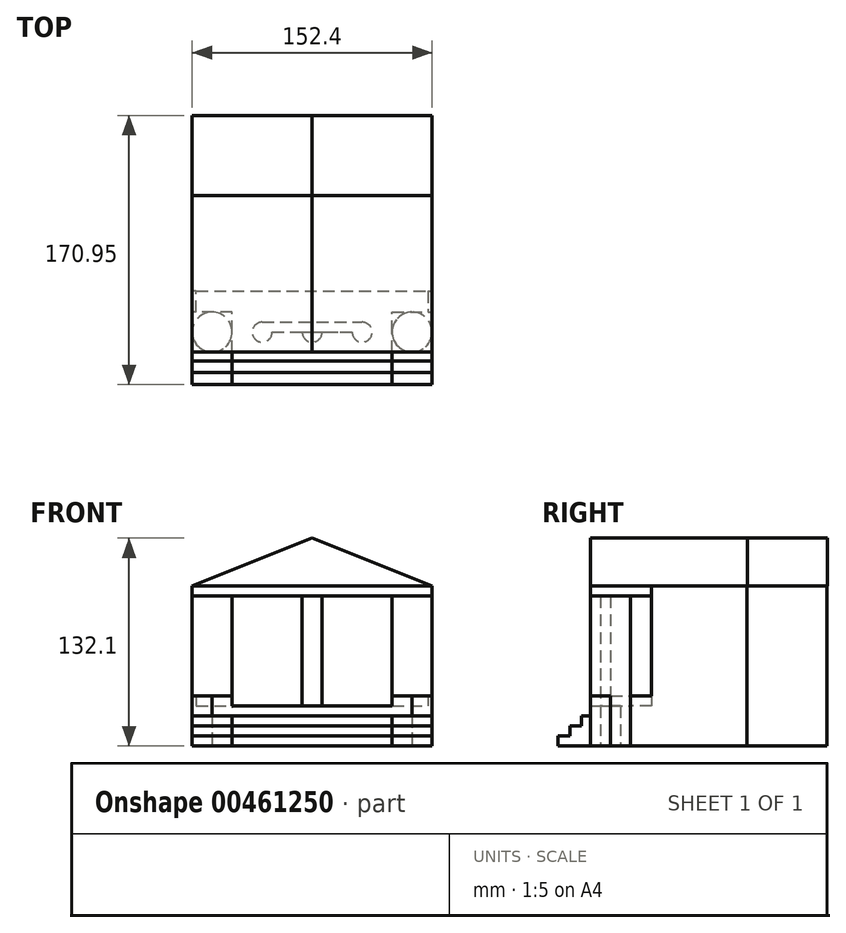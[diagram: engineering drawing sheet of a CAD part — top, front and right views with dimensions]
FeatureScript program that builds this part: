
annotation { "Feature Type Name" : "Feature", "Feature Type Description" : "" }
export const myFeature = defineFeature(function(context is Context, id is Id, definition is map)
    precondition{}
    {
        {
            var Q0;
            Q0=qCreatedBy(makeId("Top.planeOp"),FACE);
            var sketch = newSketch(context, id + "F0", { "sketchPlane" : qUnion([Q0])});
            skLineSegment(sketch, "E0.bottom", {"start": v(76.2, 49.62) * mm, "end": v(-76.2, 49.62) * mm});
            skLineSegment(sketch, "E0.top", {"start": v(76.2, -49.62) * mm, "end": v(-76.2, -49.62) * mm});
            skLineSegment(sketch, "E0.left", {"start": v(76.2, 49.62) * mm, "end": v(76.2, -49.62) * mm});
            skLineSegment(sketch, "E0.right", {"start": v(-76.2, 49.62) * mm, "end": v(-76.2, -49.62) * mm});
            skPoint(sketch, "E0.middle", {"position": v(0, 0) * mm});
            skLineSegment(sketch, "E1", {"start": v(0, -49.62) * mm, "end": v(0, 49.62) * mm});
            skLineSegment(sketch, "E2", {"start": v(-76.2, -49.62) * mm, "end": v(-50.8, -49.62) * mm});
            skLineSegment(sketch, "E3", {"start": v(76.2, -49.62) * mm, "end": v(50.8, -49.62) * mm});
            skLineSegment(sketch, "E4", {"start": v(-50.8, -49.62) * mm, "end": v(-50.8, -70.26) * mm});
            skLineSegment(sketch, "E5", {"start": v(-50.8, -70.26) * mm, "end": v(50.8, -70.26) * mm});
            skLineSegment(sketch, "E6", {"start": v(50.8, -49.62) * mm, "end": v(50.8, -70.26) * mm});
            skLineSegment(sketch, "E7", {"start": v(-50.8, -62.64) * mm, "end": v(50.8, -62.64) * mm});
            skLineSegment(sketch, "E8", {"start": v(50.8, -62.64) * mm, "end": v(50.8, -55.32) * mm});
            skLineSegment(sketch, "E9", {"start": v(50.8, -55.32) * mm, "end": v(-50.8, -55.32) * mm});
            skLineSegment(sketch, "E10", {"start": v(-50.8, -49.62) * mm, "end": v(-50.8, -24.22) * mm});
            skLineSegment(sketch, "E11", {"start": v(-50.8, -24.22) * mm, "end": v(-76.2, -24.22) * mm});
            skLineSegment(sketch, "E12", {"start": v(-76.2, -24.22) * mm, "end": v(-76.2, -49.62) * mm});
            skLineSegment(sketch, "E13", {"start": v(50.8, -49.62) * mm, "end": v(50.8, -24.22) * mm});
            skLineSegment(sketch, "E14", {"start": v(50.8, -24.22) * mm, "end": v(76.2, -24.22) * mm});
            skLineSegment(sketch, "E15", {"start": v(76.2, -24.22) * mm, "end": v(76.2, -49.62) * mm});
            skCircle(sketch, "E16", {"center": v(-63.5, -36.92) * mm, "radius": 12.7 * mm});
            skCircle(sketch, "E17", {"center": v(63.5, -36.92) * mm, "radius": 12.7 * mm});
            skLineSegment(sketch, "E18", {"start": v(-63.5, -36.92) * mm, "end": v(63.5, -36.92) * mm});
            skLineSegment(sketch, "E19", {"start": v(0, -36.92) * mm, "end": v(-63.5, -36.92) * mm});
            skLineSegment(sketch, "E20", {"start": v(-31.75, -36.92) * mm, "end": v(-31.75, -24.23) * mm});
            skLineSegment(sketch, "E21", {"start": v(0, -36.92) * mm, "end": v(63.5, -36.92) * mm});
            skLineSegment(sketch, "E22", {"start": v(31.75, -36.92) * mm, "end": v(31.75, -24.23) * mm});
            skLineSegment(sketch, "E23", {"start": v(-31.75, -30.58) * mm, "end": v(31.75, -30.58) * mm});
            skCircle(sketch, "E24", {"center": v(-31.75, -36.92) * mm, "radius": 6.35 * mm});
            skCircle(sketch, "E25", {"center": v(31.75, -36.92) * mm, "radius": 6.35 * mm});
            skCircle(sketch, "E26", {"center": v(0, -36.92) * mm, "radius": 6.35 * mm});
            skLineSegment(sketch, "E27", {"start": v(-73.66, -24.22) * mm, "end": v(-73.66, -10.82) * mm});
            skLineSegment(sketch, "E28", {"start": v(-73.66, -10.82) * mm, "end": v(73.66, -10.82) * mm});
            skLineSegment(sketch, "E29", {"start": v(73.66, -10.82) * mm, "end": v(73.66, -24.22) * mm});
            skLineSegment(sketch, "E30", {"start": v(-73.66, -24.22) * mm, "end": v(-76.2, -24.22) * mm});
            skLineSegment(sketch, "E31", {"start": v(73.66, -24.22) * mm, "end": v(76.2, -24.22) * mm});
            skLineSegment(sketch, "E32", {"start": v(73.66, -10.82) * mm, "end": v(76.2, -10.82) * mm});
            skLineSegment(sketch, "E33", {"start": v(-73.66, -10.82) * mm, "end": v(-76.2, -10.82) * mm});
            skSolve(sketch);
        }
        {
            var Q0;
            {var subQ7=sQuery(id+"F0.wireOp",EDGE,"E33");Q0=makeQuery(id+"F0.imprint","IMPRINT",FACE,{"disambiguationData":[TD([[makeQuery(id+"F0.imprint","IMPRINT",EDGE,{"derivedFrom":subQ7}),-1.0]])]});}
            var Q1;
            {var subQ0=sQuery(id+"F0.wireOp",EDGE,"E32");Q1=makeQuery(id+"F0.imprint","IMPRINT",FACE,{"disambiguationData":[TD([[makeQuery(id+"F0.imprint","IMPRINT",EDGE,{"derivedFrom":subQ0}),1.0]])]});}
            extrude(context, id + "F1", {"entities" : qUnion([Q0, Q1]), "depth" : 101.6 * mm});
        }
        {
            var Q0;
            {var subQ0=sQuery(id+"F0.wireOp",EDGE,"E27");Q0=makeQuery(id+"F0.imprint","IMPRINT",FACE,{"disambiguationData":[TD([[makeQuery(id+"F0.imprint","IMPRINT",EDGE,{"derivedFrom":subQ0}),-1.0]])]});}
            var Q1;
            {var subQ0=sQuery(id+"F0.wireOp",EDGE,"E26");var subQ1=sQuery(id+"F0.wireOp",EDGE,"E19");var subQ2=makeQuery(id+"F0.imprint","INTERSECT",VERTEX,{"derivedFrom":[subQ1,subQ0]});Q1=makeQuery(id+"F0.imprint","IMPRINT",FACE,{"disambiguationData":[TD([[makeQuery(id+"F0.imprint","IMPRINT",EDGE,{"disambiguationData":[TD([[subQ2,-1.0]])],"derivedFrom":subQ1}),-1.0]])]});}
            var Q2;
            {var subQ6=sQuery(id+"F0.wireOp",EDGE,"E0.top");var subQ8=sQuery(id+"F0.wireOp",EDGE,"E1");var subQ9=makeQuery(id+"F0.imprint","INTERSECT",VERTEX,{"derivedFrom":[subQ6,subQ8]});Q2=makeQuery(id+"F0.imprint","IMPRINT",FACE,{"disambiguationData":[TD([[makeQuery(id+"F0.imprint","IMPRINT",EDGE,{"disambiguationData":[TD([[subQ9,-1.0]])],"derivedFrom":subQ8}),1.0]])]});}
            var Q3;
            {var subQ5=sQuery(id+"F0.wireOp",EDGE,"E1");var subQ6=sQuery(id+"F0.wireOp",EDGE,"E0.top");var subQ7=makeQuery(id+"F0.imprint","INTERSECT",VERTEX,{"derivedFrom":[subQ6,subQ5]});Q3=makeQuery(id+"F0.imprint","IMPRINT",FACE,{"disambiguationData":[TD([[makeQuery(id+"F0.imprint","IMPRINT",EDGE,{"disambiguationData":[TD([[subQ7,-1.0]])],"derivedFrom":subQ5}),-1.0]])]});}
            var Q4;
            {var subQ0=sQuery(id+"F0.wireOp",EDGE,"E26");var subQ1=sQuery(id+"F0.wireOp",EDGE,"E21");var subQ2=makeQuery(id+"F0.imprint","INTERSECT",VERTEX,{"derivedFrom":[subQ1,subQ0]});Q4=makeQuery(id+"F0.imprint","IMPRINT",FACE,{"disambiguationData":[TD([[makeQuery(id+"F0.imprint","IMPRINT",EDGE,{"disambiguationData":[TD([[subQ2,-1.0]])],"derivedFrom":subQ1}),1.0]])]});}
            var Q5;
            {var subQ0=sQuery(id+"F0.wireOp",EDGE,"E29");Q5=makeQuery(id+"F0.imprint","IMPRINT",FACE,{"disambiguationData":[TD([[makeQuery(id+"F0.imprint","IMPRINT",EDGE,{"derivedFrom":subQ0}),-1.0]])]});}
            extrude(context, id + "F2", {"entities" : qUnion([Q0, Q1, Q2, Q3, Q4, Q5]), "operationType" : NewBodyOperationType.ADD, "depth" : 25.4 * mm});
        }
        {
            var Q0;
            Q0=makeQuery(id+"F0.imprint","IMPRINT",FACE,{"disambiguationData":[TD([[makeQuery(id+"F0.imprint","IMPRINT",EDGE,{"derivedFrom":sQuery(id+"F0.wireOp",EDGE,"E27")}),1.0]])]});
            var Q1;
            Q1=makeQuery(id+"F0.imprint","IMPRINT",FACE,{"disambiguationData":[TD([[makeQuery(id+"F0.imprint","IMPRINT",EDGE,{"derivedFrom":sQuery(id+"F0.wireOp",EDGE,"E29")}),1.0]])]});
            extrude(context, id + "F3", {"entities" : qUnion([Q0, Q1]), "operationType" : NewBodyOperationType.ADD, "depth" : 31.75 * mm});
        }
        {
            var Q0;
            {var subQ0=sQuery(id+"F0.wireOp",EDGE,"E19");var subQ1=makeQuery(id+"F0.imprint","INTERSECT",VERTEX,{"derivedFrom":[subQ0,sQuery(id+"F0.wireOp",EDGE,"E20")]});Q0=makeQuery(id+"F0.imprint","IMPRINT",FACE,{"disambiguationData":[TD([[makeQuery(id+"F0.imprint","IMPRINT",EDGE,{"disambiguationData":[TD([[subQ1,1.0]])],"derivedFrom":subQ0}),1.0]])]});}
            var Q1;
            {var subQ0=sQuery(id+"F0.wireOp",EDGE,"E20");var subQ1=sQuery(id+"F0.wireOp",EDGE,"E19");var subQ2=makeQuery(id+"F0.imprint","INTERSECT",VERTEX,{"derivedFrom":[subQ1,subQ0]});Q1=makeQuery(id+"F0.imprint","IMPRINT",FACE,{"disambiguationData":[TD([[makeQuery(id+"F0.imprint","IMPRINT",EDGE,{"disambiguationData":[TD([[subQ2,-1.0]])],"derivedFrom":subQ1}),-1.0]])]});}
            var Q2;
            {var subQ0=sQuery(id+"F0.wireOp",EDGE,"E20");var subQ1=sQuery(id+"F0.wireOp",EDGE,"E19");var subQ2=makeQuery(id+"F0.imprint","INTERSECT",VERTEX,{"derivedFrom":[subQ1,subQ0]});Q2=makeQuery(id+"F0.imprint","IMPRINT",FACE,{"disambiguationData":[TD([[makeQuery(id+"F0.imprint","IMPRINT",EDGE,{"disambiguationData":[TD([[subQ2,1.0]])],"derivedFrom":subQ1}),-1.0]])]});}
            var Q3;
            {var subQ0=sQuery(id+"F0.wireOp",EDGE,"E19");var subQ3=sQuery(id+"F0.wireOp",EDGE,"E26");var subQ5=makeQuery(id+"F0.imprint","INTERSECT",VERTEX,{"derivedFrom":[subQ0,subQ3]});Q3=makeQuery(id+"F0.imprint","IMPRINT",FACE,{"disambiguationData":[TD([[makeQuery(id+"F0.imprint","IMPRINT",EDGE,{"disambiguationData":[TD([[subQ5,1.0]])],"derivedFrom":subQ0}),-1.0]])]});}
            var Q4;
            {var subQ0=sQuery(id+"F0.wireOp",EDGE,"E21");var subQ3=sQuery(id+"F0.wireOp",EDGE,"E26");var subQ5=makeQuery(id+"F0.imprint","INTERSECT",VERTEX,{"derivedFrom":[subQ0,subQ3]});Q4=makeQuery(id+"F0.imprint","IMPRINT",FACE,{"disambiguationData":[TD([[makeQuery(id+"F0.imprint","IMPRINT",EDGE,{"disambiguationData":[TD([[subQ5,1.0]])],"derivedFrom":subQ0}),1.0]])]});}
            var Q5;
            {var subQ1=sQuery(id+"F0.wireOp",EDGE,"E1");var subQ3=sQuery(id+"F0.wireOp",EDGE,"E26");var subQ4=makeQuery(id+"F0.imprint","INTERSECT",VERTEX,{"derivedFrom":[subQ1,subQ3]});Q5=makeQuery(id+"F0.imprint","IMPRINT",FACE,{"disambiguationData":[TD([[makeQuery(id+"F0.imprint","IMPRINT",EDGE,{"disambiguationData":[TD([[subQ4,1.0]])],"derivedFrom":subQ3}),1.0]])]});}
            var Q6;
            {var subQ1=sQuery(id+"F0.wireOp",EDGE,"E1");var subQ3=sQuery(id+"F0.wireOp",EDGE,"E26");var subQ4=makeQuery(id+"F0.imprint","INTERSECT",VERTEX,{"derivedFrom":[subQ1,subQ3]});Q6=makeQuery(id+"F0.imprint","IMPRINT",FACE,{"disambiguationData":[TD([[makeQuery(id+"F0.imprint","IMPRINT",EDGE,{"disambiguationData":[TD([[subQ4,-1.0]])],"derivedFrom":subQ3}),1.0]])]});}
            var Q7;
            {var subQ0=sQuery(id+"F0.wireOp",EDGE,"E22");var subQ1=sQuery(id+"F0.wireOp",EDGE,"E21");var subQ2=makeQuery(id+"F0.imprint","INTERSECT",VERTEX,{"derivedFrom":[subQ1,subQ0]});Q7=makeQuery(id+"F0.imprint","IMPRINT",FACE,{"disambiguationData":[TD([[makeQuery(id+"F0.imprint","IMPRINT",EDGE,{"disambiguationData":[TD([[subQ2,1.0]])],"derivedFrom":subQ1}),1.0]])]});}
            var Q8;
            {var subQ0=sQuery(id+"F0.wireOp",EDGE,"E22");var subQ1=sQuery(id+"F0.wireOp",EDGE,"E21");var subQ2=makeQuery(id+"F0.imprint","INTERSECT",VERTEX,{"derivedFrom":[subQ1,subQ0]});Q8=makeQuery(id+"F0.imprint","IMPRINT",FACE,{"disambiguationData":[TD([[makeQuery(id+"F0.imprint","IMPRINT",EDGE,{"disambiguationData":[TD([[subQ2,-1.0]])],"derivedFrom":subQ1}),1.0]])]});}
            var Q9;
            {var subQ0=sQuery(id+"F0.wireOp",EDGE,"E21");var subQ1=makeQuery(id+"F0.imprint","INTERSECT",VERTEX,{"derivedFrom":[subQ0,sQuery(id+"F0.wireOp",EDGE,"E22")]});Q9=makeQuery(id+"F0.imprint","IMPRINT",FACE,{"disambiguationData":[TD([[makeQuery(id+"F0.imprint","IMPRINT",EDGE,{"disambiguationData":[TD([[subQ1,1.0]])],"derivedFrom":subQ0}),-1.0]])]});}
            extrude(context, id + "F4", {"entities" : qUnion([Q0, Q1, Q2, Q3, Q4, Q5, Q6, Q7, Q8, Q9]), "operationType" : NewBodyOperationType.ADD, "depth" : 95.25 * mm});
        }
        {
            var Q0;
            {var subQ0=sQuery(id+"F0.wireOp",EDGE,"E16");var subQ3=makeQuery(id+"F0.imprint","INTERSECT",VERTEX,{"derivedFrom":[sQuery(id+"F0.wireOp",EDGE,"E12"),subQ0]});Q0=makeQuery(id+"F0.imprint","IMPRINT",FACE,{"disambiguationData":[TD([[makeQuery(id+"F0.imprint","IMPRINT",EDGE,{"disambiguationData":[TD([[subQ3,1.0]])],"derivedFrom":subQ0}),1.0]])]});}
            var Q1;
            {var subQ0=sQuery(id+"F0.wireOp",EDGE,"E17");var subQ1=makeQuery(id+"F0.imprint","INTERSECT",VERTEX,{"derivedFrom":[sQuery(id+"F0.wireOp",EDGE,"E15"),subQ0]});Q1=makeQuery(id+"F0.imprint","IMPRINT",FACE,{"disambiguationData":[TD([[makeQuery(id+"F0.imprint","IMPRINT",EDGE,{"disambiguationData":[TD([[subQ1,-1.0]])],"derivedFrom":subQ0}),1.0]])]});}
            extrude(context, id + "F5", {"entities" : qUnion([Q0, Q1]), "operationType" : NewBodyOperationType.ADD, "depth" : 95.25 * mm});
        }
        {
            var Q0;
            {var subQ0=sQuery(id+"F0.wireOp",EDGE,"E30");Q0=makeQuery(id+"F0.imprint","IMPRINT",FACE,{"disambiguationData":[TD([[makeQuery(id+"F0.imprint","IMPRINT",EDGE,{"derivedFrom":subQ0}),1.0]])]});}
            var Q1;
            {var subQ0=sQuery(id+"F0.wireOp",EDGE,"E12");var subQ1=sQuery(id+"F0.wireOp",EDGE,"E2");var subQ2=makeQuery(id+"F0.imprint","INTERSECT",VERTEX,{"derivedFrom":[subQ1,subQ0]});Q1=makeQuery(id+"F0.imprint","IMPRINT",FACE,{"disambiguationData":[TD([[makeQuery(id+"F0.imprint","IMPRINT",EDGE,{"disambiguationData":[TD([[subQ2,-1.0]])],"derivedFrom":subQ1}),1.0]])]});}
            var Q2;
            {var subQ1=sQuery(id+"F0.wireOp",EDGE,"E2");var subQ3=sQuery(id+"F0.wireOp",EDGE,"E16");var subQ4=makeQuery(id+"F0.imprint","INTERSECT",VERTEX,{"derivedFrom":[subQ1,subQ3]});Q2=makeQuery(id+"F0.imprint","IMPRINT",FACE,{"disambiguationData":[TD([[makeQuery(id+"F0.imprint","IMPRINT",EDGE,{"disambiguationData":[TD([[subQ4,-1.0]])],"derivedFrom":subQ3}),-1.0]])]});}
            var Q3;
            {var subQ0=sQuery(id+"F0.wireOp",EDGE,"E11");var subQ1=sQuery(id+"F0.wireOp",EDGE,"E10");var subQ2=makeQuery(id+"F0.imprint","INTERSECT",VERTEX,{"derivedFrom":[subQ1,subQ0]});Q3=makeQuery(id+"F0.imprint","IMPRINT",FACE,{"disambiguationData":[TD([[makeQuery(id+"F0.imprint","IMPRINT",EDGE,{"disambiguationData":[TD([[subQ2,-1.0]])],"derivedFrom":subQ0}),1.0]])]});}
            var Q4;
            {var subQ0=sQuery(id+"F0.wireOp",EDGE,"E14");var subQ1=sQuery(id+"F0.wireOp",EDGE,"E13");var subQ2=makeQuery(id+"F0.imprint","INTERSECT",VERTEX,{"derivedFrom":[subQ1,subQ0]});Q4=makeQuery(id+"F0.imprint","IMPRINT",FACE,{"disambiguationData":[TD([[makeQuery(id+"F0.imprint","IMPRINT",EDGE,{"disambiguationData":[TD([[subQ2,-1.0]])],"derivedFrom":subQ0}),-1.0]])]});}
            var Q5;
            {var subQ1=sQuery(id+"F0.wireOp",EDGE,"E3");var subQ3=sQuery(id+"F0.wireOp",EDGE,"E17");var subQ4=makeQuery(id+"F0.imprint","INTERSECT",VERTEX,{"derivedFrom":[subQ1,subQ3]});Q5=makeQuery(id+"F0.imprint","IMPRINT",FACE,{"disambiguationData":[TD([[makeQuery(id+"F0.imprint","IMPRINT",EDGE,{"disambiguationData":[TD([[subQ4,1.0]])],"derivedFrom":subQ3}),-1.0]])]});}
            var Q6;
            {var subQ0=sQuery(id+"F0.wireOp",EDGE,"E15");var subQ1=sQuery(id+"F0.wireOp",EDGE,"E3");var subQ2=makeQuery(id+"F0.imprint","INTERSECT",VERTEX,{"derivedFrom":[subQ1,subQ0]});Q6=makeQuery(id+"F0.imprint","IMPRINT",FACE,{"disambiguationData":[TD([[makeQuery(id+"F0.imprint","IMPRINT",EDGE,{"disambiguationData":[TD([[subQ2,-1.0]])],"derivedFrom":subQ1}),-1.0]])]});}
            var Q7;
            {var subQ0=sQuery(id+"F0.wireOp",EDGE,"E31");Q7=makeQuery(id+"F0.imprint","IMPRINT",FACE,{"disambiguationData":[TD([[makeQuery(id+"F0.imprint","IMPRINT",EDGE,{"derivedFrom":subQ0}),-1.0]])]});}
            extrude(context, id + "F6", {"entities" : qUnion([Q0, Q1, Q2, Q3, Q4, Q5, Q6, Q7]), "depth" : 31.75 * mm});
        }
        {
            var Q0;
            {var subQ3=sQuery(id+"F0.wireOp",EDGE,"E9");Q0=makeQuery(id+"F0.imprint","IMPRINT",FACE,{"disambiguationData":[TD([[makeQuery(id+"F0.imprint","IMPRINT",EDGE,{"derivedFrom":subQ3}),-1.0]])]});}
            extrude(context, id + "F7", {"entities" : qUnion([Q0]), "operationType" : NewBodyOperationType.ADD, "depth" : 19.05 * mm});
        }
        {
            var Q0;
            {var subQ0=sQuery(id+"F0.wireOp",EDGE,"E7");Q0=makeQuery(id+"F0.imprint","IMPRINT",FACE,{"disambiguationData":[TD([[makeQuery(id+"F0.imprint","IMPRINT",EDGE,{"derivedFrom":subQ0}),1.0]])]});}
            extrude(context, id + "F8", {"entities" : qUnion([Q0]), "operationType" : NewBodyOperationType.ADD, "depth" : 12.7 * mm});
        }
        {
            var Q0;
            {var subQ0=sQuery(id+"F0.wireOp",EDGE,"E5");Q0=makeQuery(id+"F0.imprint","IMPRINT",FACE,{"disambiguationData":[TD([[makeQuery(id+"F0.imprint","IMPRINT",EDGE,{"derivedFrom":subQ0}),1.0]])]});}
            extrude(context, id + "F9", {"entities" : qUnion([Q0]), "operationType" : NewBodyOperationType.ADD, "depth" : 6.35 * mm});
        }
        {
            var Q0;
            Q0=makeQuery(id+"F1.opExtrude","SWEPT_FACE",FACE,{"disambiguationData":[OSD([sQuery(id+"F0.wireOp",EDGE,"E28"),sQuery(id+"F0.wireOp",EDGE,"E32"),sQuery(id+"F0.wireOp",EDGE,"E33")])]});
            var sketch = newSketch(context, id + "F10", { "sketchPlane" : qUnion([Q0])});
            skLineSegment(sketch, "E34", {"start": v(-76.2, 101.6) * mm, "end": v(-76.2, 95.25) * mm});
            skLineSegment(sketch, "E35", {"start": v(-76.2, 95.25) * mm, "end": v(76.2, 95.25) * mm});
            skLineSegment(sketch, "E36", {"start": v(76.2, 95.25) * mm, "end": v(76.2, 101.6) * mm});
            skLineSegment(sketch, "E37", {"start": v(76.2, 101.6) * mm, "end": v(-76.2, 101.6) * mm});
            skSolve(sketch);
        }
        {
            var Q0;
            Q0 = qSketchRegion(id + "F10", true);
            extrude(context, id + "F11", {"entities" : qUnion([Q0]), "depth" : 38.86 * mm});
        }
        {
            var Q0;
            Q0=makeQuery(id+"F11.opExtrude","CAP_FACE",FACE,{"disambiguationData":[OSD([sQuery(id+"F10.wireOp",EDGE,"E34"),sQuery(id+"F10.wireOp",EDGE,"E35"),sQuery(id+"F10.wireOp",EDGE,"E36"),sQuery(id+"F10.wireOp",EDGE,"E37")])],"isStart":false});
            var sketch = newSketch(context, id + "F12", { "sketchPlane" : qUnion([Q0])});
            skLineSegment(sketch, "E38", {"start": v(-76.2, 101.6) * mm, "end": v(0, 132.1) * mm});
            skLineSegment(sketch, "E39", {"start": v(0, 132.1) * mm, "end": v(76.2, 101.6) * mm});
            skLineSegment(sketch, "E40", {"start": v(76.2, 101.6) * mm, "end": v(-76.2, 101.6) * mm});
            skSolve(sketch);
        }
        {
            var Q0;
            Q0 = qSketchRegion(id + "F12", true);
            extrude(context, id + "F13", {"entities" : qUnion([Q0]), "oppositeDirection" : true, "depth" : 99.57 * mm});
        }
        {
            var Q0;
            Q0=makeQuery(id+"F13.opExtrude","CAP_FACE",FACE,{"disambiguationData":[OSD([sQuery(id+"F12.wireOp",EDGE,"E38"),sQuery(id+"F12.wireOp",EDGE,"E39"),sQuery(id+"F12.wireOp",EDGE,"E40")])],"isStart":false});
            var Q1;
            Q1=makeQuery(id+"F1.opExtrude","SWEPT_FACE",FACE,{"disambiguationData":[OSD([sQuery(id+"F0.wireOp",EDGE,"E0.bottom")])]});
            extrude(context, id + "F14", {"entities" : qUnion([Q0, Q1]), "depth" : 50.8 * mm});
        }
        {
            var Q0;
            {var subQ0=sQuery(id+"F0.wireOp",EDGE,"E6");Q0=makeQuery(id+"F9.boolean.opBoolean","MERGE",FACE,{"derivedFrom":[makeQuery(id+"F8.boolean.opBoolean","MERGE",FACE,{"derivedFrom":[makeQuery(id+"F7.boolean.opBoolean","MERGE",FACE,{"derivedFrom":[makeQuery(id+"F2.opExtrude","SWEPT_FACE",FACE,{"disambiguationData":[OSD([sQuery(id+"F0.wireOp",EDGE,"E13")])]}),makeQuery(id+"F7.opExtrude","SWEPT_FACE",FACE,{"disambiguationData":[OSD([subQ0])]})]}),makeQuery(id+"F8.opExtrude","SWEPT_FACE",FACE,{"disambiguationData":[OSD([sQuery(id+"F0.wireOp",EDGE,"E8")])]})]}),makeQuery(id+"F9.opExtrude","SWEPT_FACE",FACE,{"disambiguationData":[OSD([subQ0])]})]});}
            extrude(context, id + "F15", {"entities" : qUnion([Q0]), "depth" : 25.4 * mm});
        }
        {
            var Q0;
            {var subQ0=sQuery(id+"F0.wireOp",EDGE,"E4");Q0=makeQuery(id+"F9.boolean.opBoolean","MERGE",FACE,{"derivedFrom":[makeQuery(id+"F8.boolean.opBoolean","MERGE",FACE,{"derivedFrom":[makeQuery(id+"F7.boolean.opBoolean","MERGE",FACE,{"derivedFrom":[makeQuery(id+"F2.opExtrude","SWEPT_FACE",FACE,{"disambiguationData":[OSD([sQuery(id+"F0.wireOp",EDGE,"E10")])]}),makeQuery(id+"F7.opExtrude","SWEPT_FACE",FACE,{"disambiguationData":[OSD([subQ0])]})]}),makeQuery(id+"F8.opExtrude","SWEPT_FACE",FACE,{"disambiguationData":[OSD([subQ0])]})]}),makeQuery(id+"F9.opExtrude","SWEPT_FACE",FACE,{"disambiguationData":[OSD([subQ0])]})]});}
            extrude(context, id + "F16", {"entities" : qUnion([Q0]), "depth" : 25.4 * mm});
        }
    });
